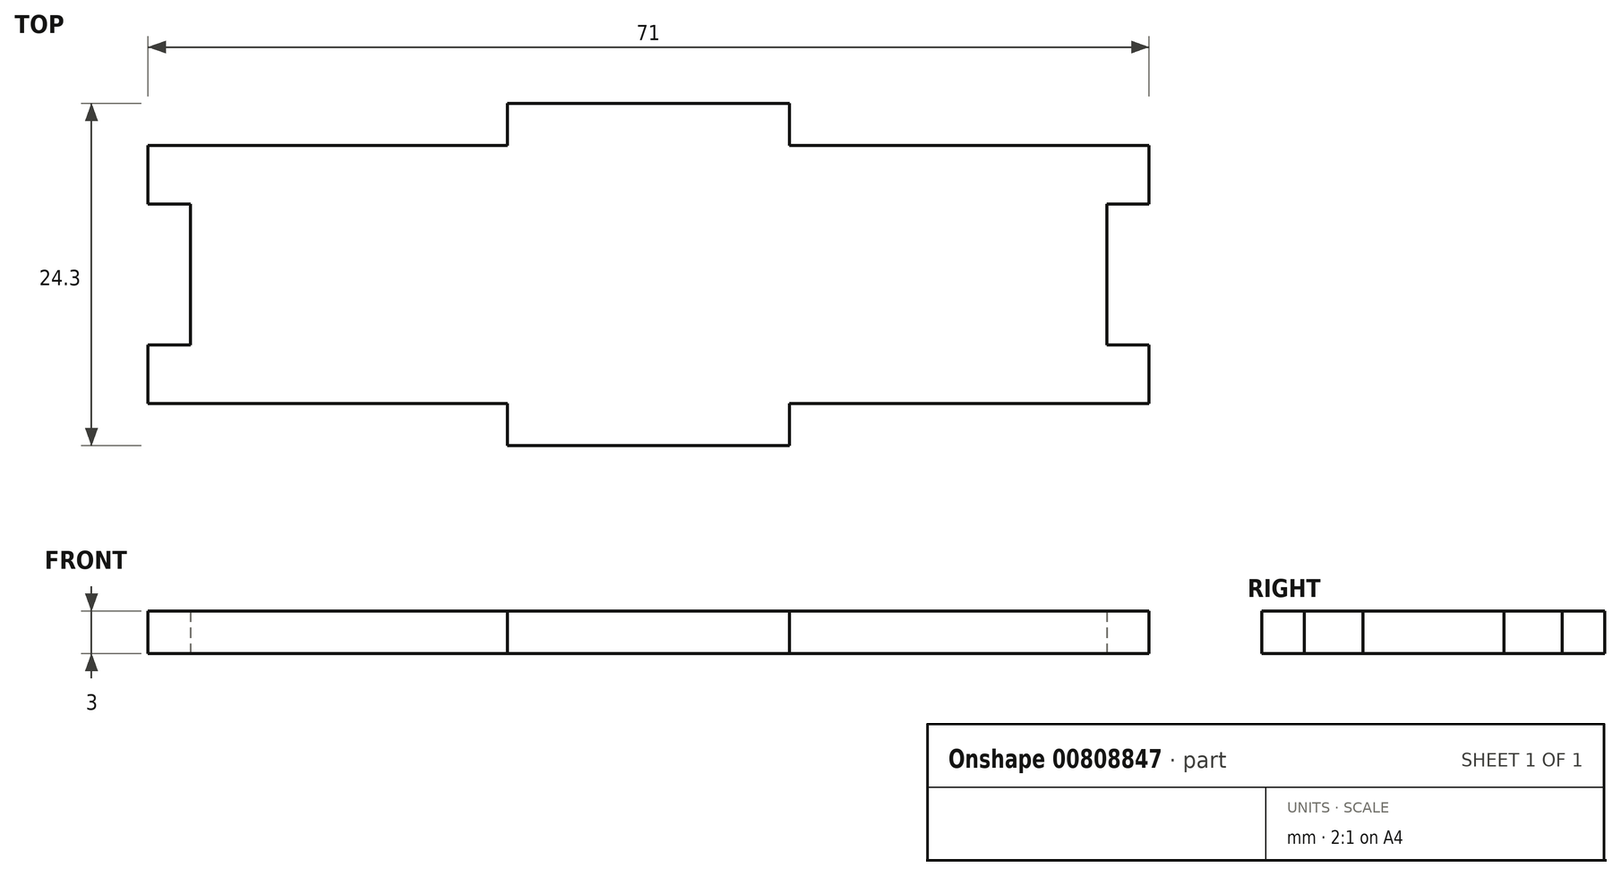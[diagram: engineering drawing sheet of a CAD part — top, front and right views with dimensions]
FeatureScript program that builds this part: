
annotation { "Feature Type Name" : "Feature", "Feature Type Description" : "" }
export const myFeature = defineFeature(function(context is Context, id is Id, definition is map)
    precondition{}
    {
        {
            var Q0;
            Q0=qCreatedBy(makeId("Top.planeOp"),FACE);
            var sketch = newSketch(context, id + "F0", { "sketchPlane" : qUnion([Q0])});
            skLineSegment(sketch, "E0.bottom", {"start": v(-35.5, 9.15) * mm, "end": v(35.5, 9.15) * mm});
            skLineSegment(sketch, "E0.top", {"start": v(-35.5, -9.15) * mm, "end": v(35.5, -9.15) * mm});
            skLineSegment(sketch, "E0.left", {"start": v(-35.5, 9.15) * mm, "end": v(-35.5, -9.15) * mm});
            skLineSegment(sketch, "E0.right", {"start": v(35.5, 9.15) * mm, "end": v(35.5, -9.15) * mm});
            skPoint(sketch, "E0.middle", {"position": v(0, 0) * mm});
            skLineSegment(sketch, "E1.bottom", {"start": v(10, -12.15) * mm, "end": v(-10, -12.15) * mm});
            skLineSegment(sketch, "E1.top", {"start": v(10, -6.15) * mm, "end": v(-10, -6.15) * mm});
            skLineSegment(sketch, "E1.left", {"start": v(10, -12.15) * mm, "end": v(10, -6.15) * mm});
            skLineSegment(sketch, "E1.right", {"start": v(-10, -12.15) * mm, "end": v(-10, -6.15) * mm});
            skPoint(sketch, "E1.middle", {"position": v(0, -9.15) * mm});
            skLineSegment(sketch, "E2.bottom", {"start": v(10, 12.15) * mm, "end": v(-10, 12.15) * mm});
            skLineSegment(sketch, "E2.top", {"start": v(10, 6.15) * mm, "end": v(-10, 6.15) * mm});
            skLineSegment(sketch, "E2.left", {"start": v(10, 12.15) * mm, "end": v(10, 6.15) * mm});
            skLineSegment(sketch, "E2.right", {"start": v(-10, 12.15) * mm, "end": v(-10, 6.15) * mm});
            skPoint(sketch, "E2.middle", {"position": v(0, 9.15) * mm});
            skLineSegment(sketch, "E3.bottom", {"start": v(-32.5, -5) * mm, "end": v(-38.5, -5) * mm});
            skLineSegment(sketch, "E3.top", {"start": v(-32.5, 5) * mm, "end": v(-38.5, 5) * mm});
            skLineSegment(sketch, "E3.left", {"start": v(-32.5, -5) * mm, "end": v(-32.5, 5) * mm});
            skLineSegment(sketch, "E3.right", {"start": v(-38.5, -5) * mm, "end": v(-38.5, 5) * mm});
            skPoint(sketch, "E3.middle", {"position": v(-35.5, 0) * mm});
            skLineSegment(sketch, "E4.bottom", {"start": v(38.5, -5) * mm, "end": v(32.5, -5) * mm});
            skLineSegment(sketch, "E4.top", {"start": v(38.5, 5) * mm, "end": v(32.5, 5) * mm});
            skLineSegment(sketch, "E4.left", {"start": v(38.5, -5) * mm, "end": v(38.5, 5) * mm});
            skLineSegment(sketch, "E4.right", {"start": v(32.5, -5) * mm, "end": v(32.5, 5) * mm});
            skPoint(sketch, "E4.middle", {"position": v(35.5, 0) * mm});
            skSolve(sketch);
        }
        {
            var Q0;
            {var subQ5=sQuery(id+"F0.wireOp",EDGE,"E2.bottom");Q0=makeQuery(id+"F0.imprint","IMPRINT",FACE,{"disambiguationData":[TD([[makeQuery(id+"F0.imprint","IMPRINT",EDGE,{"derivedFrom":subQ5}),1.0]])]});}
            var Q1;
            {var subQ5=sQuery(id+"F0.wireOp",EDGE,"E1.bottom");Q1=makeQuery(id+"F0.imprint","IMPRINT",FACE,{"disambiguationData":[TD([[makeQuery(id+"F0.imprint","IMPRINT",EDGE,{"derivedFrom":subQ5}),-1.0]])]});}
            var Q2;
            {var subQ5=sQuery(id+"F0.wireOp",EDGE,"E2.top");Q2=makeQuery(id+"F0.imprint","IMPRINT",FACE,{"disambiguationData":[TD([[makeQuery(id+"F0.imprint","IMPRINT",EDGE,{"derivedFrom":subQ5}),-1.0]])]});}
            var Q3;
            {var subQ5=sQuery(id+"F0.wireOp",EDGE,"E1.top");Q3=makeQuery(id+"F0.imprint","IMPRINT",FACE,{"disambiguationData":[TD([[makeQuery(id+"F0.imprint","IMPRINT",EDGE,{"derivedFrom":subQ5}),1.0]])]});}
            var Q4;
            {var subQ1=sQuery(id+"F0.wireOp",EDGE,"E1.top");Q4=makeQuery(id+"F0.imprint","IMPRINT",FACE,{"disambiguationData":[TD([[makeQuery(id+"F0.imprint","IMPRINT",EDGE,{"derivedFrom":subQ1}),-1.0]])]});}
            extrude(context, id + "F1", {"entities" : qUnion([Q0, Q1, Q2, Q3, Q4]), "depth" : 3 * mm, "offsetDistance" : 25 * mm});
        }
    });
